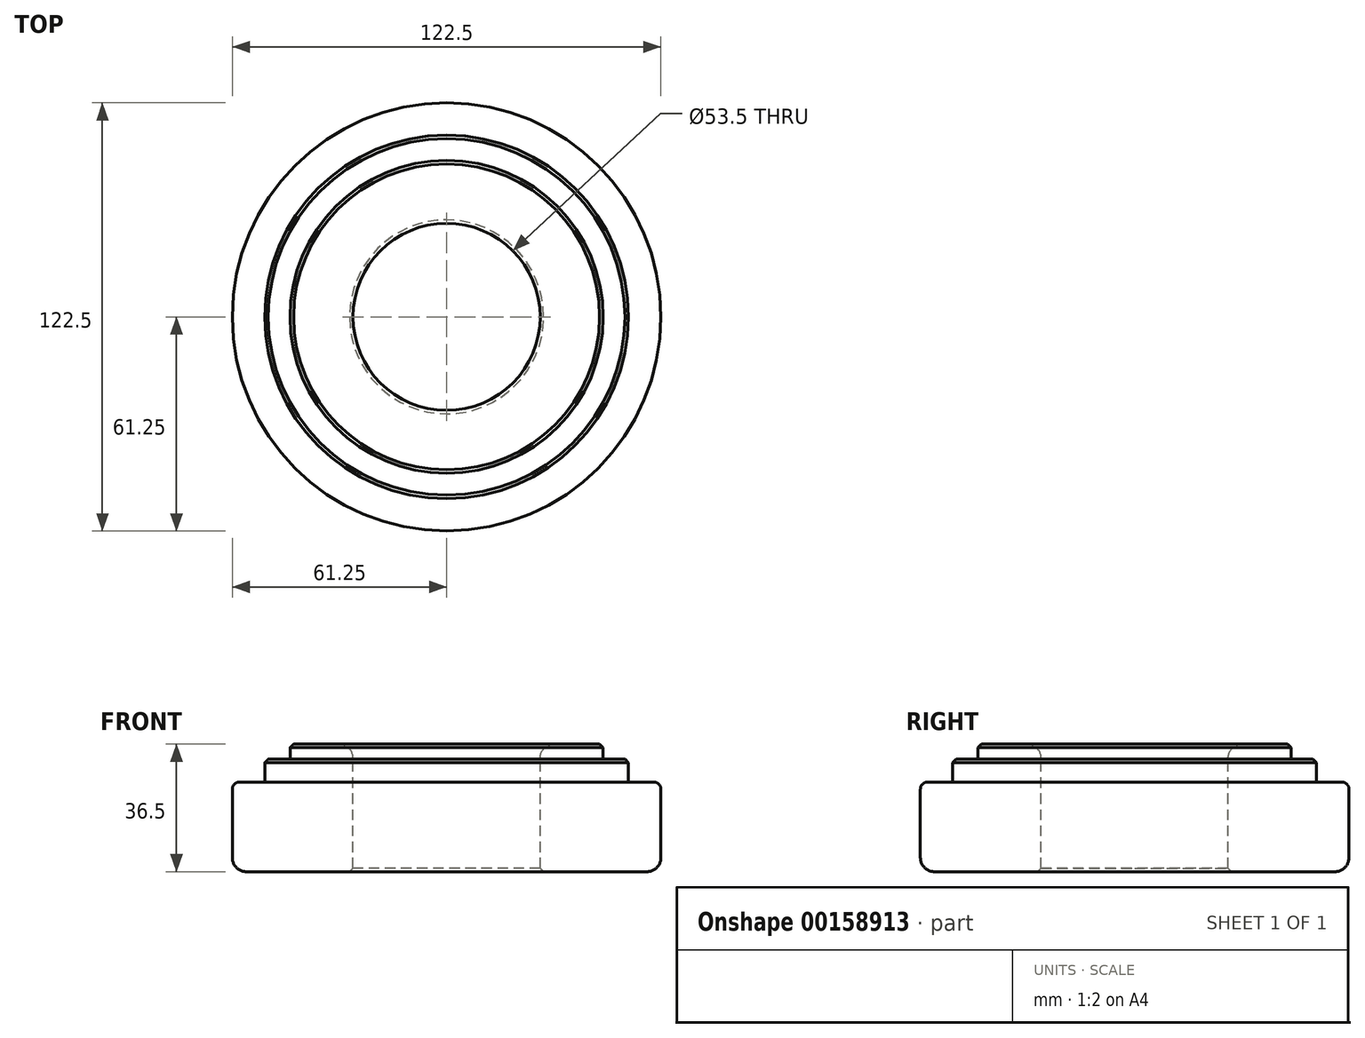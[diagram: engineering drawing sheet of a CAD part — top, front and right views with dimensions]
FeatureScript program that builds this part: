
annotation { "Feature Type Name" : "Feature", "Feature Type Description" : "" }
export const myFeature = defineFeature(function(context is Context, id is Id, definition is map)
    precondition{}
    {
        {
            var Q0;
            Q0=qCreatedBy(makeId("Front.planeOp"),FACE);
            var sketch = newSketch(context, id + "F0", { "sketchPlane" : qUnion([Q0])});
            skLineSegment(sketch, "E0", {"start": v(0, 112.23) * mm, "end": v(0, -136.93) * mm, "construction": true});
            skLineSegment(sketch, "E1", {"start": v(26.75, 18.25) * mm, "end": v(26.75, -18.25) * mm});
            skLineSegment(sketch, "E2", {"start": v(26.75, -18.25) * mm, "end": v(61.25, -18.25) * mm});
            skLineSegment(sketch, "E3", {"start": v(61.25, -18.25) * mm, "end": v(61.25, 7.38) * mm});
            skLineSegment(sketch, "E4", {"start": v(61.25, 7.38) * mm, "end": v(52, 7.38) * mm});
            skLineSegment(sketch, "E5", {"start": v(52, 13.95) * mm, "end": v(52, 7.38) * mm});
            skLineSegment(sketch, "E6", {"start": v(52, 13.95) * mm, "end": v(44.75, 13.95) * mm});
            skLineSegment(sketch, "E7", {"start": v(44.75, 18.25) * mm, "end": v(44.75, 13.95) * mm});
            skLineSegment(sketch, "E8", {"start": v(44.75, 18.25) * mm, "end": v(26.75, 18.25) * mm});
            skLineSegment(sketch, "E9", {"start": v(26.75, 0) * mm, "end": v(0, 0) * mm, "construction": true});
            skSolve(sketch);
        }
        {
            var Q0;
            Q0 = qSketchRegion(id + "F0", true);
            var Q1;
            Q1=sQuery(id+"F0.wireOp",EDGE,"E0");
            revolve(context, id + "F1", {"entities" : qUnion([Q0]), "axis" : qUnion([Q1]), "revolveType" : RevolveType.FULL});
        }
        {
            var Q0;
            Q0=makeQuery(id+"F1.opRevolve","SWEPT_EDGE",EDGE,{"disambiguationData":[OSD([sQuery(id+"F0.wireOp",EDGE,"E1"),sQuery(id+"F0.wireOp",EDGE,"E8")])]});
            var Q1;
            Q1=makeQuery(id+"F1.opRevolve","SWEPT_EDGE",EDGE,{"disambiguationData":[OSD([sQuery(id+"F0.wireOp",EDGE,"E2"),sQuery(id+"F0.wireOp",EDGE,"E3")])]});
            fillet(context, id + "F2", {"entities" : qUnion([Q0, Q1]), "radius" : 4 * mm, "tangentPropagation" : true, "allowEdgeOverflow" : false});
        }
        {
            var Q0;
            Q0=makeQuery(id+"F1.opRevolve","SWEPT_EDGE",EDGE,{"disambiguationData":[OSD([sQuery(id+"F0.wireOp",EDGE,"E3"),sQuery(id+"F0.wireOp",EDGE,"E4")])]});
            fillet(context, id + "F3", {"entities" : qUnion([Q0]), "radius" : 2 * mm, "tangentPropagation" : true, "allowEdgeOverflow" : false});
        }
        {
            var Q0;
            Q0=makeQuery(id+"F1.opRevolve","SWEPT_EDGE",EDGE,{"disambiguationData":[OSD([sQuery(id+"F0.wireOp",EDGE,"E7"),sQuery(id+"F0.wireOp",EDGE,"E8")])]});
            var Q1;
            Q1=makeQuery(id+"F1.opRevolve","SWEPT_EDGE",EDGE,{"disambiguationData":[OSD([sQuery(id+"F0.wireOp",EDGE,"E5"),sQuery(id+"F0.wireOp",EDGE,"E6")])]});
            var Q2;
            Q2=makeQuery(id+"F1.opRevolve","SWEPT_EDGE",EDGE,{"disambiguationData":[OSD([sQuery(id+"F0.wireOp",EDGE,"E1"),sQuery(id+"F0.wireOp",EDGE,"E2")])]});
            chamfer(context, id + "F4", {"entities" : qUnion([Q0, Q1, Q2]), "width" : 1 * mm, "tangentPropagation" : true});
        }
    });
